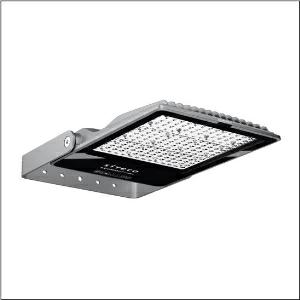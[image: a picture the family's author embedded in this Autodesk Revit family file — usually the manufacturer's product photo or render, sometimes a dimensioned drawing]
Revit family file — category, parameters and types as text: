
# Revit family: sicompact_r__31_midi___pl32_5xa7581e1k23_f752
name_source: partatom
category: Lighting Fixtures
units: mm (PartAtom-declared; Revit-internal decimal feet)

## family parameters
Cut with Voids When Loaded = No
Host = Face
Light Source = No
Part Type = Normal
Room Calculation Point = No
Round Connector Dimension = Use Diameter
Shared = No

## types (1)
- SiCompact® 31 midi  PL32 (1 x LED, 37000 lm, 250 W, 3000K)
    Apparent Load = 250 VA
    CIE Flux Codes = 32 69 98 100 100
    Color Rendering = 70
    Color Temperature = 3000K
    Default Elevation = 1800 mm
    Description = SiCompact® 31 midi, floodlight, primary light control with lens, of plastic, of toughened safety glass, transparent, light distribution: PL32, light emission: direct distribution, primary light characteristic: asymmetric, installation type: surface-mounted, LED, High Power LED, rated luminous flux: 37.000lm, luminous efficacy: 148lm/W, light colour: 730, colour temperature: 3000K, control gear: ECG, with cable, 3x 1.5mm², mains connection: 220..240V, AC, 50/60Hz, connection cable pre-assembled, cable length: 2m, rated input power: 250W, of diecast aluminium, specular, metallic grey (RAL 9006), length: 560mm, width: 330mm, height: 62mm, bracket, of sheet steel, coated, metallic grey (RAL 9006), ON/OFF, protection rating (complete): IP66, insulation class (complete): insulation class I (protective earthing), certification: CE, ENEC, impact resistance: IK08, permissible operating ambient temperature: -40..+45°C, packaging unit: 1 piece

Light Distribution: PL32
    Height = 62 mm  [stored 0.203412 ft]
    Lamp = 1 x LED
    Lamp Light Flux = 37000 lm
    Lamp Power = 250 W
    Lamp count = 1
    Length = 560 mm
    Luminous efficacy = 148 lm/W
    Manufacturer = Siteco
    ModVariant = No
    Model = 5XA7581E1K23
    Mounting Place = Wall
    Mounting Type = Surface mounted
    Number of Poles = 1
    OnlyDefault = Yes
    Power Factor = 1
    Product Name = SiCompact® 31 midi | PL32
    Product group = floodlight | wall mounted
    ProductGroupID = 2001
    Protection Class = Protection class I
    Protection Degree = IP 66
    RLX_Detail_Level = 1
    RLX_Emergency_Light_Flux = 0 lm
    RLX_Emergency_Type = 0
    RLX_Emergency_Type_DB = No
    RlxData = <blob elided: 98193 chars, md5=ba1fabc2>
    Socket = socket
    Standby Power = 0 W
    System Light Flux = 37000 lm
    System Power = 250 W
    Type Comments = Product without accessories
    Type Image = l_1006415.jpg
    URL = http://relux.com
    VarID = ---
    Voltage = 0 V
    Weight = 0.00 kg
    Width = 333 mm

note: [stored X ft] marks values corroborated as IEEE doubles in the binary element streams (Revit-internal decimal feet)

## geometry (parser evidence)
native form markers: Blend x4, Sweep x12
no freeform markers — native parametric forms only
